# Revit family: НЕВАТОМ_Вентилятор VO с панелью, версия 1
name_source: partatom
category: Оборудование
revit_build: Autodesk Revit 2017 (Build: 20170118_1100(x64)
units: mm (PartAtom-declared; Revit-internal decimal feet)

## family parameters
Всегда вертикально = Да
На основе рабочей плоскости = Нет
Общий = Нет
При загрузке вырезать с полостями = Нет
Размер круглого соединителя = Использовать диаметр
Тип детали = Нормальный
Точка расчета площади = Нет

## types (14) — shared parameters
ADSK_Единица измерения = шт.
ADSK_Завод-изготовитель = НЕВАТОМ
ADSK_Количество = 1
ADSK_Материал наименование = Оцинкованная сталь
ADSK_Наименование = Вентилятор осевой
Nevatom_URL = https://t.me

## per-type parameters (varying)
| type | ADSK_Марка | ADSK_Масса | ADSK_Масса_Текст | ADSK_Напряжение | ADSK_Полная мощность | ADSK_Размер_Высота | ADSK_Размер_Длина | ADSK_Размер_Ширина | ADSK_Ток | ADSK_Частота вращения вентилятора | B | D | D верх вент | D осн вент | D* | D1 | D1.1 | D2 | D2.1 | А | С |
| VO 200-4E | VO 200-4Е-03 | 1.9 | 1.9 кг | 230 В | 0 кВт | 312 мм | 312 мм | 52 мм | 0 А | 1460 | 312 мм | 205 мм | 26 мм | 41 мм | 17 мм | 191 мм | 150 мм | 137 мм | 96 мм | 260 мм | 52 мм |
| VO 250-4E | VO 250-4Е-03 | 2.5 | 2.5 кг | 230 В | 0 кВт | 370 мм | 370 мм | 55 мм | 0 А | 1380 | 370 мм | 260 мм | 33 мм | 52 мм | 22 мм | 243 мм | 191 мм | 173 мм | 121 мм | 320 мм | 55 мм |
| VO 300-4Е | VO 300-4Е-03 | 3.2 | 3.2 кг | 230 В | 0 кВт | 430 мм | 430 мм | 80 мм | 0 А | 1370 | 430 мм | 315 мм | 39 мм | 63 мм | 26 мм | 294 мм | 231 мм | 210 мм | 147 мм | 380 мм | 80 мм |
| VO 350-4Е | VO 350-4Е-03 | 4.7 | 4.7 кг | 230 В | 0 кВт | 485 мм | 485 мм | 85 мм | 1 А | 1370 | 485 мм | 360 мм | 45 мм | 72 мм | 30 мм | 336 мм | 264 мм | 240 мм | 168 мм | 435 мм | 85 мм |
| VO 400-4Е | VO 400-4Е-03 | 6.1 | 6.1 кг | 230 В | 0 кВт | 540 мм | 540 мм | 100 мм | 1 А | 1350 | 540 мм | 410 мм | 51 мм | 82 мм | 34 мм | 383 мм | 301 мм | 273 мм | 191 мм | 490 мм | 100 мм |
| VO 450-4E | VO 450-4Е-03 | 6.9 | 6.9 кг | 230 В | 0 кВт | 575 мм | 575 мм | 100 мм | 1 А | 1380 | 575 мм | 460 мм | 58 мм | 92 мм | 38 мм | 429 мм | 337 мм | 307 мм | 215 мм | 535 мм | 100 мм |
| VO 400-4D | VO 400-4D-03 | 6.1 | 6.1 кг | 380 В | 0 кВт | 540 мм | 540 мм | 100 мм | 0 А | 1380 | 540 мм | 410 мм | 51 мм | 82 мм | 34 мм | 383 мм | 301 мм | 273 мм | 191 мм | 490 мм | 100 мм |
| VO 450-4D | VO 450-4D-03 | 6.9 | 6.9 кг | 380 В | 0 кВт | 575 мм | 575 мм | 100 мм | 1 А | 1400 | 575 мм | 460 мм | 58 мм | 92 мм | 38 мм | 429 мм | 337 мм | 307 мм | 215 мм | 535 мм | 100 мм |
| VO 500-4E | VO 500-4E-03 | 9.5 | 9.5 кг | 230 В | 0 кВт | 655 мм | 655 мм | 120 мм | 2 А | 1320 | 655 мм | 510 мм | 64 мм | 102 мм | 43 мм | 476 мм | 374 мм | 340 мм | 238 мм | 615 мм | 120 мм |
| VO 500-4D | VO 500-4D-03 | 9.5 | 9.5 кг | 380 В | 0 кВт | 655 мм | 655 мм | 120 мм | 1 А | 1320 | 655 мм | 510 мм | 64 мм | 102 мм | 43 мм | 476 мм | 374 мм | 340 мм | 238 мм | 615 мм | 120 мм |
| VO 560-4E | VO 560-4E-03 | 10.5 | 10.5 кг | 230 В | 1 кВт | 725 мм | 725 мм | 135 мм | 2 А | 1310 | 725 мм | 560 мм | 70 мм | 112 мм | 47 мм | 523 мм | 411 мм | 373 мм | 261 мм | 675 мм | 135 мм |
| VO 560-4D | VO 560-4D-03 | 10.5 | 10.5 кг | 380 В | 1 кВт | 725 мм | 725 мм | 135 мм | 1 А | 1300 | 725 мм | 560 мм | 70 мм | 112 мм | 47 мм | 523 мм | 411 мм | 373 мм | 261 мм | 675 мм | 135 мм |
| VO 630-4E | VO 630-4E-03 | 15 | 15.0 кг | 230 В | 1 кВт | 805 мм | 805 мм | 150 мм | 4 А | 1315 | 805 мм | 630 мм | 79 мм | 126 мм | 53 мм | 588 мм | 462 мм | 420 мм | 294 мм | 750 мм | 150 мм |
| VO 630-4D | VO 630-6D-03 | 15 | 15.0 кг | 380 В | 1 кВт | 805 мм | 805 мм | 150 мм | 2 А | 1365 | 805 мм | 630 мм | 79 мм | 126 мм | 53 мм | 588 мм | 462 мм | 420 мм | 294 мм | 750 мм | 150 мм |
